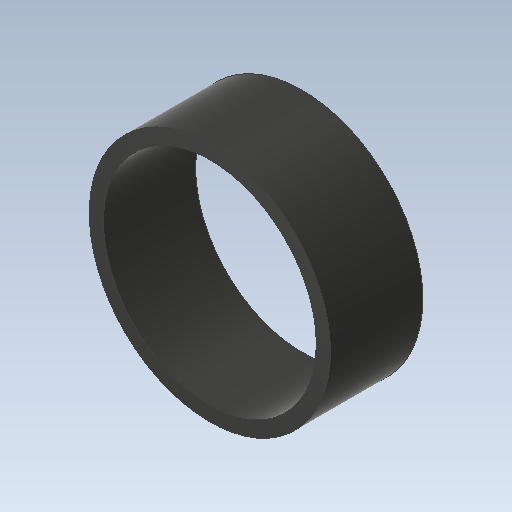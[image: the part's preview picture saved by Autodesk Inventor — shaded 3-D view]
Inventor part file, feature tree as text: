
AUTODESK INVENTOR PART (.ipt)
format: ipt  version: 2020.2 (Build 242310000, 310)  size: 100,352 bytes
history: native  units: mm
features: other x1, sketch x1, extrude x1
ambient origin geometry x8: Origin, YZ Plane, XZ Plane, XY Plane, X Axis, Y Axis, Z Axis, Center Point
bodies: Body1 (feature_tree)
feature tree (3):
  other  "ソリッド1"
  sketch  "スケッチ1"
  extrude  "押し出し1"  Depth=15.0mm
